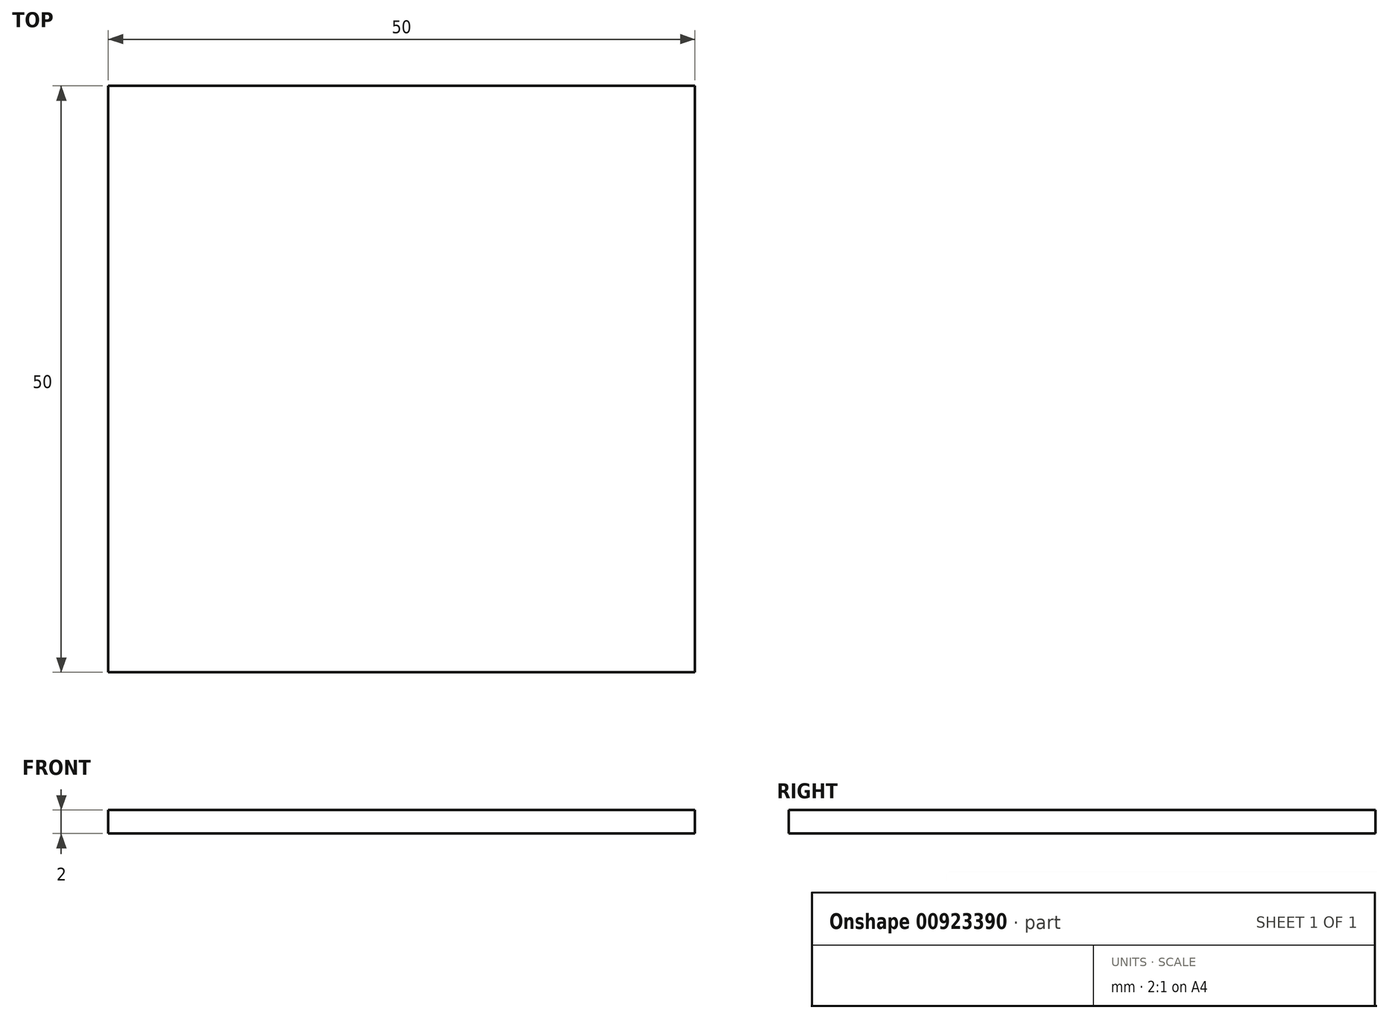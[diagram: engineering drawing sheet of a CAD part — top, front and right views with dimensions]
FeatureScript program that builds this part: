
annotation { "Feature Type Name" : "Feature", "Feature Type Description" : "" }
export const myFeature = defineFeature(function(context is Context, id is Id, definition is map)
    precondition{}
    {
        {
            var Q0;
            Q0=qCreatedBy(makeId("Top.planeOp"),FACE);
            var sketch = newSketch(context, id + "F0", { "sketchPlane" : qUnion([Q0])});
            skLineSegment(sketch, "E0.bottom", {"start": v(28.56, -13.79) * mm, "end": v(-21.44, -13.79) * mm});
            skLineSegment(sketch, "E0.top", {"start": v(28.56, 36.21) * mm, "end": v(-21.44, 36.21) * mm});
            skLineSegment(sketch, "E0.left", {"start": v(28.56, -13.79) * mm, "end": v(28.56, 36.21) * mm});
            skLineSegment(sketch, "E0.right", {"start": v(-21.44, -13.79) * mm, "end": v(-21.44, 36.21) * mm});
            skPoint(sketch, "E0.middle", {"position": v(3.56, 11.21) * mm});
            skSolve(sketch);
        }
        {
            var Q0;
            Q0=makeQuery(id+"F0.imprint","IMPRINT",FACE,{"disambiguationData":[TD([[makeQuery(id+"F0.imprint","IMPRINT",EDGE,{"derivedFrom":sQuery(id+"F0.wireOp",EDGE,"E0.bottom")}),-1.0]])]});
            extrude(context, id + "F1", {"entities" : qUnion([Q0]), "depth" : 2 * mm, "offsetDistance" : 25.4 * mm});
        }
    });
